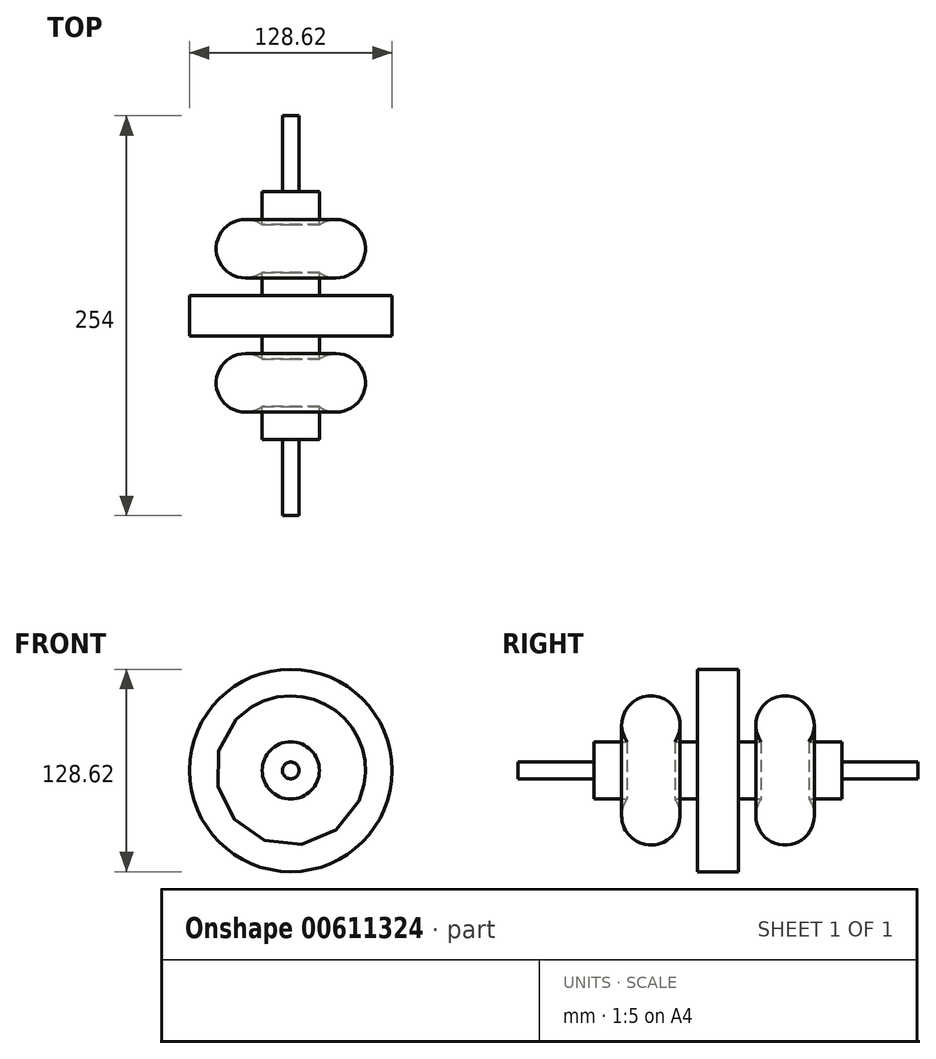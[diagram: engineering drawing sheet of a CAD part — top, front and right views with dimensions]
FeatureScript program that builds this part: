
annotation { "Feature Type Name" : "Feature", "Feature Type Description" : "" }
export const myFeature = defineFeature(function(context is Context, id is Id, definition is map)
    precondition{}
    {
        {
            var Q0;
            Q0=qCreatedBy(makeId("Front.planeOp"),FACE);
            var sketch = newSketch(context, id + "F0", { "sketchPlane" : qUnion([Q0])});
            skLineSegment(sketch, "E0", {"start": v(0, 0) * mm, "end": v(111.03, 0) * mm, "construction": true});
            skCircle(sketch, "E1", {"center": v(0, 0) * mm, "radius": 5.32 * mm});
            skLineSegment(sketch, "E2", {"start": v(0, 0) * mm, "end": v(0, 59.7) * mm, "construction": true});
            skSolve(sketch);
        }
        {
            var Q0;
            Q0 = qSketchRegion(id + "F0", true);
            extrude(context, id + "F1", {"entities" : qUnion([Q0]), "endBound" : BoundingType.SYMMETRIC, "depth" : 254 * mm, "offsetDistance" : 25.4 * mm});
        }
        {
            var Q0;
            Q0=qCreatedBy(makeId("Right.planeOp"),FACE);
            var sketch = newSketch(context, id + "F2", { "sketchPlane" : qUnion([Q0])});
            skLineSegment(sketch, "E3", {"start": v(0, 0) * mm, "end": v(-99.23, 0) * mm, "construction": true});
            skLineSegment(sketch, "E4", {"start": v(0, 0) * mm, "end": v(0, 64.3) * mm, "construction": true});
            skLineSegment(sketch, "E5", {"start": v(-78.72, 0) * mm, "end": v(-78.72, 18.16) * mm});
            skLineSegment(sketch, "E6", {"start": v(-78.72, 18.16) * mm, "end": v(-57.78, 18.16) * mm});
            skLineSegment(sketch, "E7.MirrorCS", {"start": v(78.72, 18.16) * mm, "end": v(57.78, 18.16) * mm});
            skLineSegment(sketch, "E8.MirrorCS", {"start": v(78.72, 0) * mm, "end": v(78.72, 18.16) * mm});
            skLineSegment(sketch, "E9", {"start": v(0, 64.3) * mm, "end": v(-12.92, 64.3) * mm});
            skLineSegment(sketch, "E10", {"start": v(-12.92, 64.3) * mm, "end": v(-12.92, 18.16) * mm});
            skLineSegment(sketch, "E11", {"start": v(-12.92, 18.16) * mm, "end": v(-27.45, 18.16) * mm});
            skArc(sketch, "E12", {"start": v(-27.45, 18.16) * mm, "mid": v(-42.62, 47.42) * mm, "end": v(-57.78, 18.16) * mm});
            skArc(sketch, "E13.MirrorCS", {"start": v(27.45, 18.16) * mm, "mid": v(42.62, 47.42) * mm, "end": v(57.78, 18.16) * mm});
            skLineSegment(sketch, "E14.MirrorCS", {"start": v(12.92, 64.3) * mm, "end": v(12.92, 18.16) * mm});
            skLineSegment(sketch, "E15.MirrorCS", {"start": v(12.92, 18.16) * mm, "end": v(27.45, 18.16) * mm});
            skLineSegment(sketch, "E16.MirrorCS", {"start": v(0, 64.3) * mm, "end": v(12.92, 64.3) * mm});
            skLineSegment(sketch, "E17", {"start": v(78.72, 0) * mm, "end": v(-78.72, 0) * mm});
            skSolve(sketch);
        }
        {
            var Q0;
            Q0 = qSketchRegion(id + "F2", true);
            var Q1;
            Q1=sQuery(id+"F2.wireOp",EDGE,"E17");
            revolve(context, id + "F3", {"operationType" : NewBodyOperationType.ADD, "entities" : qUnion([Q0]), "axis" : qUnion([Q1]), "revolveType" : RevolveType.FULL});
        }
    });
